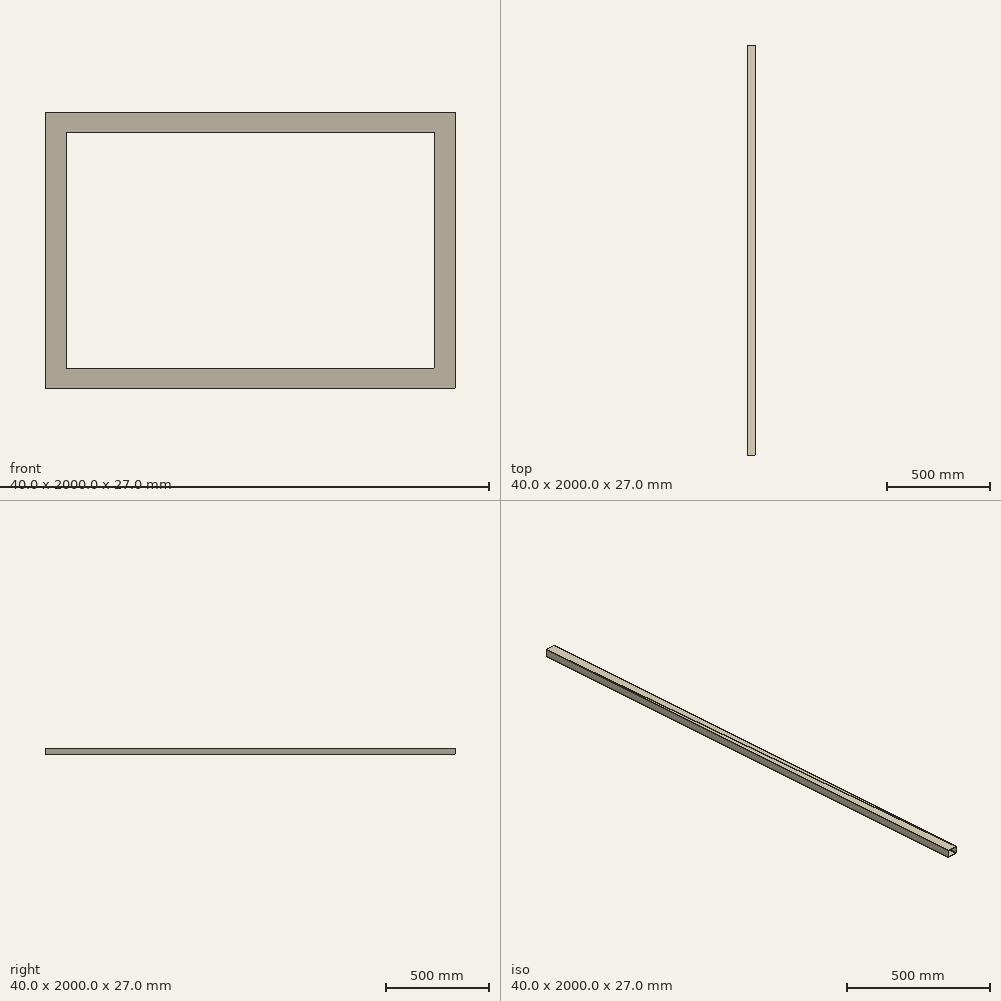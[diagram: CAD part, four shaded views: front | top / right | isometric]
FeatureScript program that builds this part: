
annotation { "Feature Type Name" : "Feature", "Feature Type Description" : "" }
export const myFeature = defineFeature(function(context is Context, id is Id, definition is map)
    precondition{}
    {
        {
            assignVariable(context, id + "F0", {"name" : "longueur", "anyValue" : 2000});
        }
        {
            var Q0;
            Q0=qCreatedBy(makeId("Front.planeOp"),FACE);
            var sketch = newSketch(context, id + "F1", { "sketchPlane" : qUnion([Q0])});
            skLineSegment(sketch, "E0.rect.bottom", {"start": v(18, 11.5) * mm, "end": v(-18, 11.5) * mm});
            skLineSegment(sketch, "E0.rect.top", {"start": v(18, -11.5) * mm, "end": v(-18, -11.5) * mm});
            skLineSegment(sketch, "E0.rect.left", {"start": v(18, 11.5) * mm, "end": v(18, -11.5) * mm});
            skLineSegment(sketch, "E0.rect.right", {"start": v(-18, 11.5) * mm, "end": v(-18, -11.5) * mm});
            skPoint(sketch, "E0.rect.middle", {"position": v(0, 0) * mm});
            skLineSegment(sketch, "E1.rect.bottom", {"start": v(20, 13.5) * mm, "end": v(-20, 13.5) * mm});
            skLineSegment(sketch, "E1.rect.top", {"start": v(20, -13.5) * mm, "end": v(-20, -13.5) * mm});
            skLineSegment(sketch, "E1.rect.left", {"start": v(20, 13.5) * mm, "end": v(20, -13.5) * mm});
            skLineSegment(sketch, "E1.rect.right", {"start": v(-20, 13.5) * mm, "end": v(-20, -13.5) * mm});
            skSolve(sketch);
        }
        {
            var Q0;
            Q0=makeQuery(id+"F1.imprint","IMPRINT",FACE,{"disambiguationData":[TD([[makeQuery(id+"F1.imprint","IMPRINT",EDGE,{"derivedFrom":sQuery(id+"F1.wireOp",EDGE,"E0.rect.bottom")}),-1.0]])]});
            extrude(context, id + "F2", {"entities" : qUnion([Q0]), "endBound" : BoundingType.SYMMETRIC, "depth" : (getVariable(context, 'longueur')) * mm, "hasSecondDirection" : true, "secondDirectionOppositeDirection" : true, "secondDirectionDepth" : (getVariable(context, 'longueur')) / 2 * mm});
        }
    });
